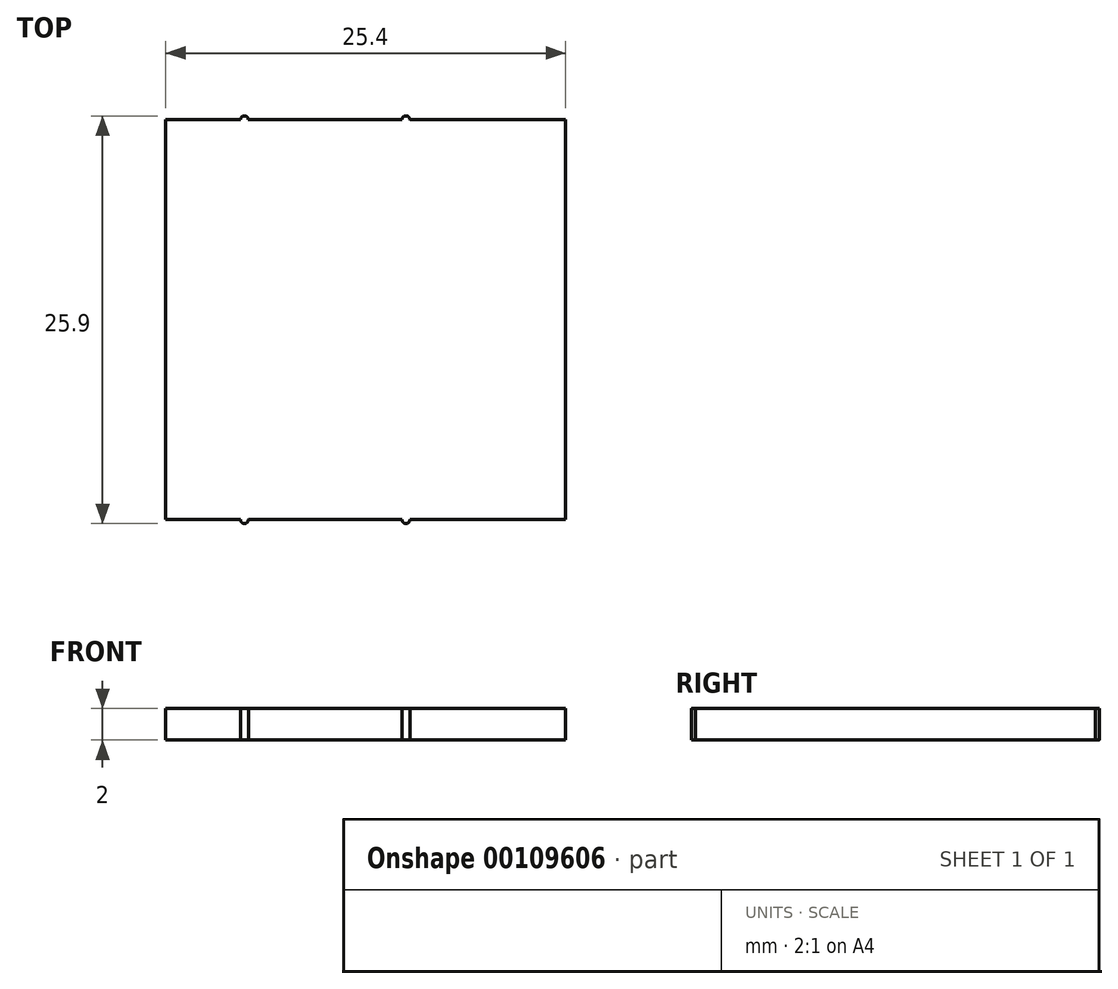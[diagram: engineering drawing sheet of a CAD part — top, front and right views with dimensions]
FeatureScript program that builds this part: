
annotation { "Feature Type Name" : "Feature", "Feature Type Description" : "" }
export const myFeature = defineFeature(function(context is Context, id is Id, definition is map)
    precondition{}
    {
        {
            var Q0;
            Q0=qCreatedBy(makeId("Top.planeOp"),FACE);
            var sketch = newSketch(context, id + "F0", { "sketchPlane" : qUnion([Q0])});
            skLineSegment(sketch, "E0.bottom", {"start": v(12.7, -12.7) * mm, "end": v(-12.7, -12.7) * mm});
            skLineSegment(sketch, "E0.top", {"start": v(12.7, 12.7) * mm, "end": v(-12.7, 12.7) * mm});
            skLineSegment(sketch, "E0.left", {"start": v(12.7, -12.7) * mm, "end": v(12.7, 12.7) * mm});
            skLineSegment(sketch, "E0.right", {"start": v(-12.7, -12.7) * mm, "end": v(-12.7, 12.7) * mm});
            skPoint(sketch, "E0.middle", {"position": v(0, 0) * mm});
            skLineSegment(sketch, "E1", {"start": v(-7.7, 12.7) * mm, "end": v(-7.7, -12.7) * mm});
            skLineSegment(sketch, "E2", {"start": v(2.56, 12.7) * mm, "end": v(2.56, -12.7) * mm});
            skLineSegment(sketch, "E3", {"start": v(-2.7, 12.7) * mm, "end": v(-2.7, -12.7) * mm});
            skLineSegment(sketch, "E4.0", {"start": v(-3.2, 12.7) * mm, "end": v(-3.2, -12.7) * mm});
            skLineSegment(sketch, "E5.0", {"start": v(-2.2, 12.7) * mm, "end": v(-2.2, -12.7) * mm});
            skArc(sketch, "E6.0.startCap", {"start": v(-7.95, 12.7) * mm, "mid": v(-7.7, 12.95) * mm, "end": v(-7.45, 12.7) * mm});
            skArc(sketch, "E6.0.endCap", {"start": v(-7.45, -12.7) * mm, "mid": v(-7.7, -12.95) * mm, "end": v(-7.95, -12.7) * mm});
            skLineSegment(sketch, "E6.0.left", {"start": v(-7.45, 12.7) * mm, "end": v(-7.45, -12.7) * mm});
            skLineSegment(sketch, "E6.0.right", {"start": v(-7.95, 12.7) * mm, "end": v(-7.95, -12.7) * mm});
            skArc(sketch, "E7.0.startCap", {"start": v(2.3, 12.7) * mm, "mid": v(2.56, 12.95) * mm, "end": v(2.8, 12.7) * mm});
            skArc(sketch, "E7.0.endCap", {"start": v(2.8, -12.7) * mm, "mid": v(2.56, -12.95) * mm, "end": v(2.3, -12.7) * mm});
            skLineSegment(sketch, "E7.0.left", {"start": v(2.8, 12.7) * mm, "end": v(2.8, -12.7) * mm});
            skLineSegment(sketch, "E7.0.right", {"start": v(2.3, 12.7) * mm, "end": v(2.3, -12.7) * mm});
            skSolve(sketch);
        }
        {
            var Q0;
            Q0 = qSketchRegion(id + "F0", true);
            extrude(context, id + "F1", {"entities" : qUnion([Q0]), "depth" : 2 * mm});
        }
    });
